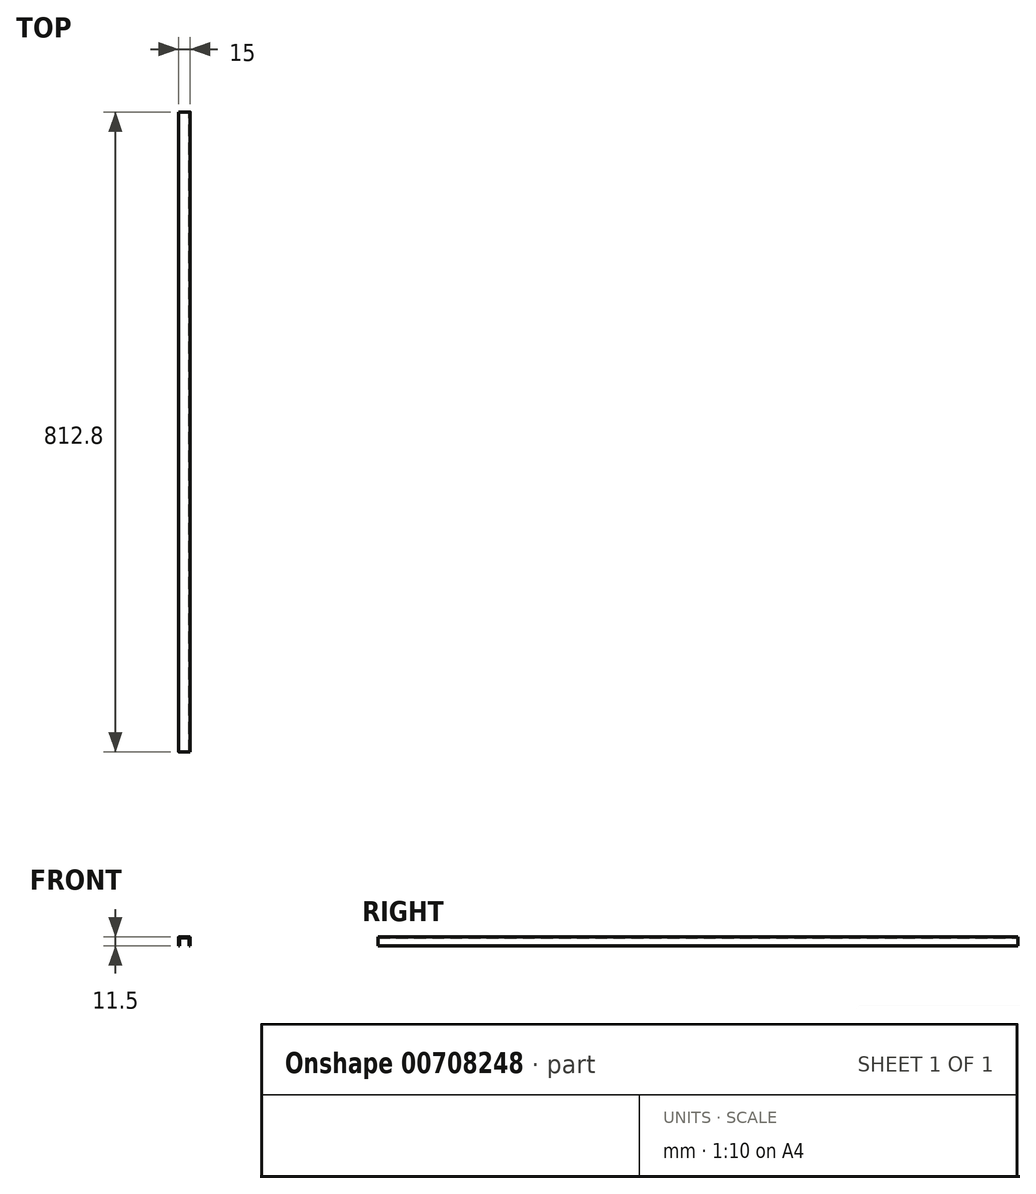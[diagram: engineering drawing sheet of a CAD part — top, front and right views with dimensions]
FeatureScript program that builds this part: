
annotation { "Feature Type Name" : "Feature", "Feature Type Description" : "" }
export const myFeature = defineFeature(function(context is Context, id is Id, definition is map)
    precondition{}
    {
        {
            var Q0;
            Q0=qCreatedBy(makeId("Front.planeOp"),FACE);
            var sketch = newSketch(context, id + "F0", { "sketchPlane" : qUnion([Q0])});
            skLineSegment(sketch, "E0", {"start": v(0, 11.5) * mm, "end": v(-6.5, 11.5) * mm});
            skLineSegment(sketch, "E1", {"start": v(-7.5, 10.5) * mm, "end": v(-7.5, 0) * mm});
            skLineSegment(sketch, "E2", {"start": v(-7.5, 0) * mm, "end": v(-6, 0) * mm});
            skLineSegment(sketch, "E3", {"start": v(-6, 0) * mm, "end": v(-6, 7) * mm});
            skLineSegment(sketch, "E4", {"start": v(-3, 10) * mm, "end": v(0, 10) * mm});
            skPoint(sketch, "E5.visualSharp", {"position": v(-7.5, 11.5) * mm});
            skArc(sketch, "E5.filletArc", {"start": v(-6.5, 11.5) * mm, "mid": v(-7.2, 11.2) * mm, "end": v(-7.5, 10.5) * mm});
            skPoint(sketch, "E6.visualSharp", {"position": v(-6, 10) * mm});
            skArc(sketch, "E6.filletArc", {"start": v(-3, 10) * mm, "mid": v(-5.12, 9.12) * mm, "end": v(-6, 7) * mm});
            skPoint(sketch, "E7.visualSharp", {"position": v(-7.5, 3) * mm});
            skLineSegment(sketch, "E8.MirrorCS", {"start": v(3, 10) * mm, "end": v(0, 10) * mm});
            skLineSegment(sketch, "E9.MirrorCS", {"start": v(0, 11.5) * mm, "end": v(6.5, 11.5) * mm});
            skArc(sketch, "E10.MirrorCS", {"start": v(3, 10) * mm, "mid": v(5.12, 9.12) * mm, "end": v(6, 7) * mm});
            skArc(sketch, "E11.MirrorCS", {"start": v(6.5, 11.5) * mm, "mid": v(7.2, 11.2) * mm, "end": v(7.5, 10.5) * mm});
            skLineSegment(sketch, "E12.MirrorCS", {"start": v(7.5, 10.5) * mm, "end": v(7.5, 0) * mm});
            skLineSegment(sketch, "E13.MirrorCS", {"start": v(6, 0) * mm, "end": v(6, 7) * mm});
            skLineSegment(sketch, "E14.MirrorCS", {"start": v(7.5, 0) * mm, "end": v(6, 0) * mm});
            skPoint(sketch, "E15.MirrorCS.end.orphan", {"position": v(7.5, 0) * mm});
            skPoint(sketch, "E15.MirrorCS.start.orphan", {"position": v(10.5, 3) * mm});
            skPoint(sketch, "E16.MirrorCS.end.orphan", {"position": v(13.3, 3) * mm});
            skPoint(sketch, "E17.start.orphan", {"position": v(-10.5, 3) * mm});
            skPoint(sketch, "E18.start.orphan", {"position": v(-13.3, 3) * mm});
            skSolve(sketch);
        }
        {
            var Q0;
            Q0=makeQuery(id+"F0.imprint","IMPRINT",FACE,{"disambiguationData":[TD([[makeQuery(id+"F0.imprint","IMPRINT",EDGE,{"derivedFrom":sQuery(id+"F0.wireOp",EDGE,"E0")}),1.0]])]});
            extrude(context, id + "F1", {"entities" : qUnion([Q0]), "depth" : 812.8 * mm, "offsetDistance" : 25 * mm});
        }
    });
